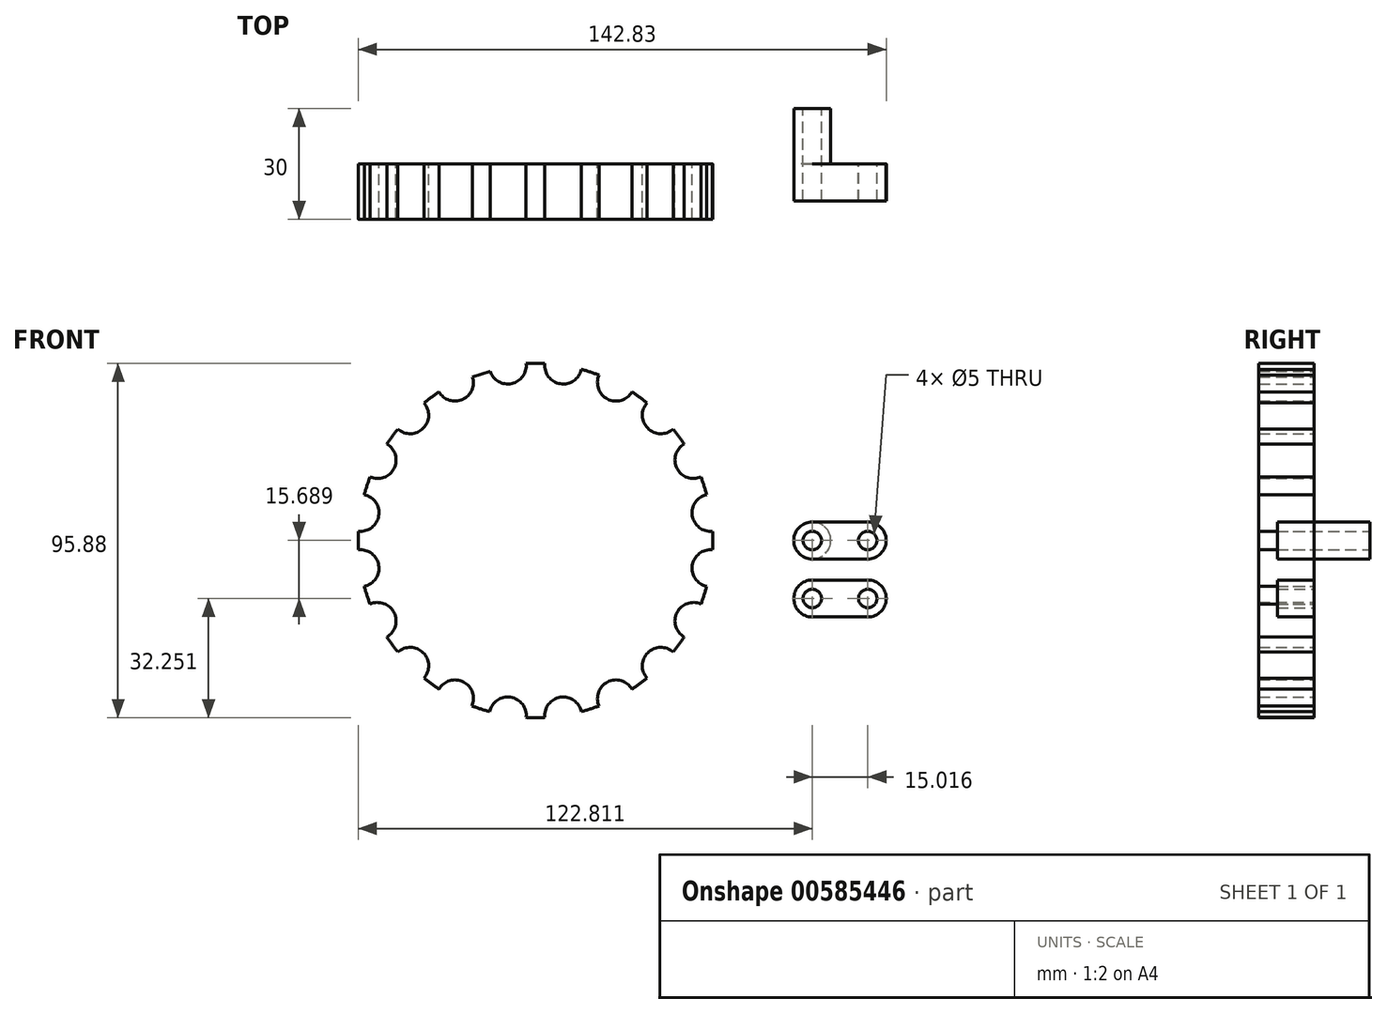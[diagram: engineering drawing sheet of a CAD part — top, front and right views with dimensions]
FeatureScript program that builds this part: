
annotation { "Feature Type Name" : "Feature", "Feature Type Description" : "" }
export const myFeature = defineFeature(function(context is Context, id is Id, definition is map)
    precondition{}
    {
        {
            var Q0;
            Q0=qCreatedBy(makeId("Front.planeOp"),FACE);
            var sketch = newSketch(context, id + "F0", { "sketchPlane" : qUnion([Q0])});
            skCircle(sketch, "E0.cCircle", {"center": v(0, 0) * mm, "radius": 47.35 * mm, "construction": true});
            skLineSegment(sketch, "E0.0", {"start": v(47.35, 7.5) * mm, "end": v(47.35, -7.5) * mm});
            skLineSegment(sketch, "E0.1", {"start": v(47.35, -7.5) * mm, "end": v(42.72, -21.77) * mm});
            skLineSegment(sketch, "E0.2", {"start": v(42.72, -21.77) * mm, "end": v(33.9, -33.9) * mm});
            skLineSegment(sketch, "E0.3", {"start": v(33.9, -33.9) * mm, "end": v(21.77, -42.72) * mm});
            skLineSegment(sketch, "E0.4", {"start": v(21.77, -42.72) * mm, "end": v(7.5, -47.35) * mm});
            skLineSegment(sketch, "E0.5", {"start": v(7.5, -47.35) * mm, "end": v(-7.5, -47.35) * mm});
            skLineSegment(sketch, "E0.6", {"start": v(-7.5, -47.35) * mm, "end": v(-21.77, -42.72) * mm});
            skLineSegment(sketch, "E0.7", {"start": v(-21.77, -42.72) * mm, "end": v(-33.9, -33.9) * mm});
            skLineSegment(sketch, "E0.8", {"start": v(-33.9, -33.9) * mm, "end": v(-42.72, -21.77) * mm});
            skLineSegment(sketch, "E0.9", {"start": v(-42.72, -21.77) * mm, "end": v(-47.35, -7.5) * mm});
            skLineSegment(sketch, "E0.10", {"start": v(-47.35, -7.5) * mm, "end": v(-47.35, 7.5) * mm});
            skLineSegment(sketch, "E0.11", {"start": v(-47.35, 7.5) * mm, "end": v(-42.72, 21.77) * mm});
            skLineSegment(sketch, "E0.12", {"start": v(-42.72, 21.77) * mm, "end": v(-33.9, 33.9) * mm});
            skLineSegment(sketch, "E0.13", {"start": v(-33.9, 33.9) * mm, "end": v(-21.77, 42.72) * mm});
            skLineSegment(sketch, "E0.14", {"start": v(-21.77, 42.72) * mm, "end": v(-7.5, 47.35) * mm});
            skLineSegment(sketch, "E0.15", {"start": v(-7.5, 47.35) * mm, "end": v(7.5, 47.35) * mm});
            skLineSegment(sketch, "E0.16", {"start": v(7.5, 47.35) * mm, "end": v(21.77, 42.72) * mm});
            skLineSegment(sketch, "E0.17", {"start": v(21.77, 42.72) * mm, "end": v(33.9, 33.9) * mm});
            skLineSegment(sketch, "E0.18", {"start": v(33.9, 33.9) * mm, "end": v(42.72, 21.77) * mm});
            skLineSegment(sketch, "E0.19", {"start": v(42.72, 21.77) * mm, "end": v(47.35, 7.5) * mm});
            skPoint(sketch, "E0.0.midPoint", {"position": v(47.35, 0) * mm});
            skCircle(sketch, "E1", {"center": v(47.35, 7.5) * mm, "radius": 5 * mm});
            skCircle(sketch, "E2.1.0", {"center": v(42.72, 21.77) * mm, "radius": 5 * mm});
            skCircle(sketch, "E2.2.0", {"center": v(33.9, 33.9) * mm, "radius": 5 * mm});
            skCircle(sketch, "E2.3.0", {"center": v(21.77, 42.72) * mm, "radius": 5 * mm});
            skCircle(sketch, "E3.1.4.0", {"center": v(7.5, 47.35) * mm, "radius": 5 * mm});
            skCircle(sketch, "E3.1.5.0", {"center": v(-7.5, 47.35) * mm, "radius": 5 * mm});
            skCircle(sketch, "E3.1.6.0", {"center": v(-21.77, 42.72) * mm, "radius": 5 * mm});
            skCircle(sketch, "E3.1.7.0", {"center": v(-33.9, 33.9) * mm, "radius": 5 * mm});
            skCircle(sketch, "E3.1.8.0", {"center": v(-42.72, 21.77) * mm, "radius": 5 * mm});
            skCircle(sketch, "E3.1.9.0", {"center": v(-47.35, 7.5) * mm, "radius": 5 * mm});
            skCircle(sketch, "E3.1.10.0", {"center": v(-47.35, -7.5) * mm, "radius": 5 * mm});
            skCircle(sketch, "E3.1.11.0", {"center": v(-42.72, -21.77) * mm, "radius": 5 * mm});
            skCircle(sketch, "E3.1.12.0", {"center": v(-33.9, -33.9) * mm, "radius": 5 * mm});
            skCircle(sketch, "E3.1.13.0", {"center": v(-21.77, -42.72) * mm, "radius": 5 * mm});
            skCircle(sketch, "E3.1.14.0", {"center": v(-7.5, -47.35) * mm, "radius": 5 * mm});
            skCircle(sketch, "E3.1.15.0", {"center": v(7.5, -47.35) * mm, "radius": 5 * mm});
            skCircle(sketch, "E3.1.16.0", {"center": v(21.77, -42.72) * mm, "radius": 5 * mm});
            skCircle(sketch, "E3.1.17.0", {"center": v(33.9, -33.9) * mm, "radius": 5 * mm});
            skCircle(sketch, "E3.1.18.0", {"center": v(42.72, -21.77) * mm, "radius": 5 * mm});
            skCircle(sketch, "E3.1.19.0", {"center": v(47.35, -7.5) * mm, "radius": 5 * mm});
            skCircle(sketch, "E4", {"center": v(74.87, 0) * mm, "radius": 5 * mm});
            skCircle(sketch, "E5", {"center": v(89.87, 0) * mm, "radius": 5 * mm});
            skLineSegment(sketch, "E6", {"start": v(74.87, 0) * mm, "end": v(89.87, 0) * mm, "construction": true});
            skLineSegment(sketch, "E7.bottom", {"start": v(74.87, 5) * mm, "end": v(89.87, 5) * mm});
            skLineSegment(sketch, "E7.top", {"start": v(74.87, -5) * mm, "end": v(89.87, -5) * mm});
            skLineSegment(sketch, "E7.left", {"start": v(74.87, 5) * mm, "end": v(74.87, -5) * mm});
            skLineSegment(sketch, "E7.right", {"start": v(89.87, 5) * mm, "end": v(89.87, -5) * mm});
            skCircle(sketch, "E8", {"center": v(74.87, 0) * mm, "radius": 2.5 * mm});
            skCircle(sketch, "E9", {"center": v(89.87, 0) * mm, "radius": 2.5 * mm});
            skCircle(sketch, "E10", {"center": v(74.89, -15.69) * mm, "radius": 2.5 * mm});
            skCircle(sketch, "E11", {"center": v(74.89, -15.69) * mm, "radius": 5 * mm});
            skLineSegment(sketch, "E12", {"start": v(74.89, -15.69) * mm, "end": v(89.89, -15.69) * mm, "construction": true});
            skCircle(sketch, "E13", {"center": v(89.89, -15.69) * mm, "radius": 5 * mm});
            skCircle(sketch, "E14", {"center": v(89.89, -15.69) * mm, "radius": 2.5 * mm});
            skLineSegment(sketch, "E15.bottom", {"start": v(74.89, -10.69) * mm, "end": v(89.89, -10.69) * mm});
            skLineSegment(sketch, "E15.top", {"start": v(74.89, -20.69) * mm, "end": v(89.89, -20.69) * mm});
            skLineSegment(sketch, "E15.left", {"start": v(74.89, -10.69) * mm, "end": v(74.89, -20.69) * mm});
            skLineSegment(sketch, "E15.right", {"start": v(89.89, -10.69) * mm, "end": v(89.89, -20.69) * mm});
            skCircle(sketch, "E16", {"center": v(0, 0) * mm, "radius": 47.94 * mm});
            skSolve(sketch);
        }
        {
            var Q0;
            {var subQ3=sQuery(id+"F0.wireOp",EDGE,"E1");var subQ39=sQuery(id+"F0.wireOp",EDGE,"E0.0");var subQ40=makeQuery(id+"F0.imprint","INTERSECT",VERTEX,{"derivedFrom":[subQ39,subQ3]});Q0=makeQuery(id+"F0.imprint","IMPRINT",FACE,{"disambiguationData":[TD([[makeQuery(id+"F0.imprint","IMPRINT",EDGE,{"disambiguationData":[TD([[subQ40,-1.0]])],"derivedFrom":subQ39}),-1.0]])]});}
            var Q1;
            {var subQ0=sQuery(id+"F0.wireOp",EDGE,"E2.1.0");var subQ1=sQuery(id+"F0.wireOp",EDGE,"E0.19");var subQ2=makeQuery(id+"F0.imprint","INTERSECT",VERTEX,{"derivedFrom":[subQ1,subQ0]});Q1=makeQuery(id+"F0.imprint","IMPRINT",FACE,{"disambiguationData":[TD([[makeQuery(id+"F0.imprint","IMPRINT",EDGE,{"disambiguationData":[TD([[subQ2,-1.0]])],"derivedFrom":subQ1}),1.0]])]});}
            var Q2;
            {var subQ0=sQuery(id+"F0.wireOp",EDGE,"E1");var subQ1=sQuery(id+"F0.wireOp",EDGE,"E0.0");var subQ2=makeQuery(id+"F0.imprint","INTERSECT",VERTEX,{"derivedFrom":[subQ1,subQ0]});Q2=makeQuery(id+"F0.imprint","IMPRINT",FACE,{"disambiguationData":[TD([[makeQuery(id+"F0.imprint","IMPRINT",EDGE,{"disambiguationData":[TD([[subQ2,-1.0]])],"derivedFrom":subQ1}),1.0]])]});}
            var Q3;
            {var subQ0=sQuery(id+"F0.wireOp",EDGE,"E2.2.0");var subQ1=sQuery(id+"F0.wireOp",EDGE,"E0.18");var subQ2=makeQuery(id+"F0.imprint","INTERSECT",VERTEX,{"derivedFrom":[subQ1,subQ0]});Q3=makeQuery(id+"F0.imprint","IMPRINT",FACE,{"disambiguationData":[TD([[makeQuery(id+"F0.imprint","IMPRINT",EDGE,{"disambiguationData":[TD([[subQ2,-1.0]])],"derivedFrom":subQ1}),1.0]])]});}
            var Q4;
            {var subQ0=sQuery(id+"F0.wireOp",EDGE,"E2.3.0");var subQ1=sQuery(id+"F0.wireOp",EDGE,"E0.17");var subQ2=makeQuery(id+"F0.imprint","INTERSECT",VERTEX,{"derivedFrom":[subQ1,subQ0]});Q4=makeQuery(id+"F0.imprint","IMPRINT",FACE,{"disambiguationData":[TD([[makeQuery(id+"F0.imprint","IMPRINT",EDGE,{"disambiguationData":[TD([[subQ2,-1.0]])],"derivedFrom":subQ1}),1.0]])]});}
            var Q5;
            {var subQ0=sQuery(id+"F0.wireOp",EDGE,"E3.1.4.0");var subQ1=sQuery(id+"F0.wireOp",EDGE,"E0.16");var subQ2=makeQuery(id+"F0.imprint","INTERSECT",VERTEX,{"derivedFrom":[subQ1,subQ0]});Q5=makeQuery(id+"F0.imprint","IMPRINT",FACE,{"disambiguationData":[TD([[makeQuery(id+"F0.imprint","IMPRINT",EDGE,{"disambiguationData":[TD([[subQ2,-1.0]])],"derivedFrom":subQ1}),1.0]])]});}
            var Q6;
            {var subQ0=sQuery(id+"F0.wireOp",EDGE,"E3.1.5.0");var subQ1=sQuery(id+"F0.wireOp",EDGE,"E0.15");var subQ2=makeQuery(id+"F0.imprint","INTERSECT",VERTEX,{"derivedFrom":[subQ1,subQ0]});Q6=makeQuery(id+"F0.imprint","IMPRINT",FACE,{"disambiguationData":[TD([[makeQuery(id+"F0.imprint","IMPRINT",EDGE,{"disambiguationData":[TD([[subQ2,-1.0]])],"derivedFrom":subQ1}),1.0]])]});}
            var Q7;
            {var subQ0=sQuery(id+"F0.wireOp",EDGE,"E3.1.7.0");var subQ1=sQuery(id+"F0.wireOp",EDGE,"E0.13");var subQ2=makeQuery(id+"F0.imprint","INTERSECT",VERTEX,{"derivedFrom":[subQ1,subQ0]});Q7=makeQuery(id+"F0.imprint","IMPRINT",FACE,{"disambiguationData":[TD([[makeQuery(id+"F0.imprint","IMPRINT",EDGE,{"disambiguationData":[TD([[subQ2,-1.0]])],"derivedFrom":subQ1}),1.0]])]});}
            var Q8;
            {var subQ0=sQuery(id+"F0.wireOp",EDGE,"E3.1.8.0");var subQ1=sQuery(id+"F0.wireOp",EDGE,"E0.12");var subQ2=makeQuery(id+"F0.imprint","INTERSECT",VERTEX,{"derivedFrom":[subQ1,subQ0]});Q8=makeQuery(id+"F0.imprint","IMPRINT",FACE,{"disambiguationData":[TD([[makeQuery(id+"F0.imprint","IMPRINT",EDGE,{"disambiguationData":[TD([[subQ2,-1.0]])],"derivedFrom":subQ1}),1.0]])]});}
            var Q9;
            {var subQ0=sQuery(id+"F0.wireOp",EDGE,"E3.1.9.0");var subQ1=sQuery(id+"F0.wireOp",EDGE,"E0.11");var subQ2=makeQuery(id+"F0.imprint","INTERSECT",VERTEX,{"derivedFrom":[subQ1,subQ0]});Q9=makeQuery(id+"F0.imprint","IMPRINT",FACE,{"disambiguationData":[TD([[makeQuery(id+"F0.imprint","IMPRINT",EDGE,{"disambiguationData":[TD([[subQ2,-1.0]])],"derivedFrom":subQ1}),1.0]])]});}
            var Q10;
            {var subQ0=sQuery(id+"F0.wireOp",EDGE,"E3.1.10.0");var subQ1=sQuery(id+"F0.wireOp",EDGE,"E0.10");var subQ2=makeQuery(id+"F0.imprint","INTERSECT",VERTEX,{"derivedFrom":[subQ1,subQ0]});Q10=makeQuery(id+"F0.imprint","IMPRINT",FACE,{"disambiguationData":[TD([[makeQuery(id+"F0.imprint","IMPRINT",EDGE,{"disambiguationData":[TD([[subQ2,-1.0]])],"derivedFrom":subQ1}),1.0]])]});}
            var Q11;
            {var subQ0=sQuery(id+"F0.wireOp",EDGE,"E3.1.11.0");var subQ1=sQuery(id+"F0.wireOp",EDGE,"E0.9");var subQ2=makeQuery(id+"F0.imprint","INTERSECT",VERTEX,{"derivedFrom":[subQ1,subQ0]});Q11=makeQuery(id+"F0.imprint","IMPRINT",FACE,{"disambiguationData":[TD([[makeQuery(id+"F0.imprint","IMPRINT",EDGE,{"disambiguationData":[TD([[subQ2,-1.0]])],"derivedFrom":subQ1}),1.0]])]});}
            var Q12;
            {var subQ0=sQuery(id+"F0.wireOp",EDGE,"E3.1.12.0");var subQ1=sQuery(id+"F0.wireOp",EDGE,"E0.8");var subQ2=makeQuery(id+"F0.imprint","INTERSECT",VERTEX,{"derivedFrom":[subQ1,subQ0]});Q12=makeQuery(id+"F0.imprint","IMPRINT",FACE,{"disambiguationData":[TD([[makeQuery(id+"F0.imprint","IMPRINT",EDGE,{"disambiguationData":[TD([[subQ2,-1.0]])],"derivedFrom":subQ1}),1.0]])]});}
            var Q13;
            {var subQ0=sQuery(id+"F0.wireOp",EDGE,"E3.1.13.0");var subQ1=sQuery(id+"F0.wireOp",EDGE,"E0.7");var subQ2=makeQuery(id+"F0.imprint","INTERSECT",VERTEX,{"derivedFrom":[subQ1,subQ0]});Q13=makeQuery(id+"F0.imprint","IMPRINT",FACE,{"disambiguationData":[TD([[makeQuery(id+"F0.imprint","IMPRINT",EDGE,{"disambiguationData":[TD([[subQ2,-1.0]])],"derivedFrom":subQ1}),1.0]])]});}
            var Q14;
            {var subQ0=sQuery(id+"F0.wireOp",EDGE,"E3.1.14.0");var subQ1=sQuery(id+"F0.wireOp",EDGE,"E0.6");var subQ2=makeQuery(id+"F0.imprint","INTERSECT",VERTEX,{"derivedFrom":[subQ1,subQ0]});Q14=makeQuery(id+"F0.imprint","IMPRINT",FACE,{"disambiguationData":[TD([[makeQuery(id+"F0.imprint","IMPRINT",EDGE,{"disambiguationData":[TD([[subQ2,-1.0]])],"derivedFrom":subQ1}),1.0]])]});}
            var Q15;
            {var subQ0=sQuery(id+"F0.wireOp",EDGE,"E3.1.15.0");var subQ1=sQuery(id+"F0.wireOp",EDGE,"E0.5");var subQ2=makeQuery(id+"F0.imprint","INTERSECT",VERTEX,{"derivedFrom":[subQ1,subQ0]});Q15=makeQuery(id+"F0.imprint","IMPRINT",FACE,{"disambiguationData":[TD([[makeQuery(id+"F0.imprint","IMPRINT",EDGE,{"disambiguationData":[TD([[subQ2,-1.0]])],"derivedFrom":subQ1}),1.0]])]});}
            var Q16;
            {var subQ0=sQuery(id+"F0.wireOp",EDGE,"E3.1.16.0");var subQ1=sQuery(id+"F0.wireOp",EDGE,"E0.4");var subQ2=makeQuery(id+"F0.imprint","INTERSECT",VERTEX,{"derivedFrom":[subQ1,subQ0]});Q16=makeQuery(id+"F0.imprint","IMPRINT",FACE,{"disambiguationData":[TD([[makeQuery(id+"F0.imprint","IMPRINT",EDGE,{"disambiguationData":[TD([[subQ2,-1.0]])],"derivedFrom":subQ1}),1.0]])]});}
            var Q17;
            {var subQ0=sQuery(id+"F0.wireOp",EDGE,"E3.1.17.0");var subQ1=sQuery(id+"F0.wireOp",EDGE,"E0.3");var subQ2=makeQuery(id+"F0.imprint","INTERSECT",VERTEX,{"derivedFrom":[subQ1,subQ0]});Q17=makeQuery(id+"F0.imprint","IMPRINT",FACE,{"disambiguationData":[TD([[makeQuery(id+"F0.imprint","IMPRINT",EDGE,{"disambiguationData":[TD([[subQ2,-1.0]])],"derivedFrom":subQ1}),1.0]])]});}
            var Q18;
            {var subQ0=sQuery(id+"F0.wireOp",EDGE,"E3.1.18.0");var subQ1=sQuery(id+"F0.wireOp",EDGE,"E0.2");var subQ2=makeQuery(id+"F0.imprint","INTERSECT",VERTEX,{"derivedFrom":[subQ1,subQ0]});Q18=makeQuery(id+"F0.imprint","IMPRINT",FACE,{"disambiguationData":[TD([[makeQuery(id+"F0.imprint","IMPRINT",EDGE,{"disambiguationData":[TD([[subQ2,-1.0]])],"derivedFrom":subQ1}),1.0]])]});}
            var Q19;
            {var subQ0=sQuery(id+"F0.wireOp",EDGE,"E3.1.19.0");var subQ1=sQuery(id+"F0.wireOp",EDGE,"E0.1");var subQ2=makeQuery(id+"F0.imprint","INTERSECT",VERTEX,{"derivedFrom":[subQ1,subQ0]});Q19=makeQuery(id+"F0.imprint","IMPRINT",FACE,{"disambiguationData":[TD([[makeQuery(id+"F0.imprint","IMPRINT",EDGE,{"disambiguationData":[TD([[subQ2,-1.0]])],"derivedFrom":subQ1}),1.0]])]});}
            extrude(context, id + "F1", {"entities" : qUnion([Q0, Q1, Q2, Q3, Q4, Q5, Q6, Q7, Q8, Q9, Q10, Q11, Q12, Q13, Q14, Q15, Q16, Q17, Q18, Q19]), "depth" : 15 * mm, "offsetDistance" : 25 * mm});
        }
        {
            var Q0;
            {var subQ1=sQuery(id+"F0.wireOp",EDGE,"E7.bottom");Q0=makeQuery(id+"F0.imprint","IMPRINT",FACE,{"disambiguationData":[TD([[makeQuery(id+"F0.imprint","IMPRINT",EDGE,{"derivedFrom":subQ1}),-1.0]])]});}
            var Q1;
            {var subQ0=sQuery(id+"F0.wireOp",EDGE,"E7.left");var subQ4=sQuery(id+"F0.wireOp",EDGE,"E8");var subQ5=makeQuery(id+"F0.imprint","INTERSECT",VERTEX,{"disambiguationData":[OD(0.0)],"derivedFrom":[subQ0,subQ4]});Q1=makeQuery(id+"F0.imprint","IMPRINT",FACE,{"disambiguationData":[TD([[makeQuery(id+"F0.imprint","IMPRINT",EDGE,{"disambiguationData":[TD([[subQ5,1.0]])],"derivedFrom":subQ4}),-1.0]])]});}
            var Q2;
            {var subQ0=sQuery(id+"F0.wireOp",EDGE,"E7.left");var subQ4=sQuery(id+"F0.wireOp",EDGE,"E8");var subQ5=makeQuery(id+"F0.imprint","INTERSECT",VERTEX,{"disambiguationData":[OD(0.0)],"derivedFrom":[subQ0,subQ4]});Q2=makeQuery(id+"F0.imprint","IMPRINT",FACE,{"disambiguationData":[TD([[makeQuery(id+"F0.imprint","IMPRINT",EDGE,{"disambiguationData":[TD([[subQ5,-1.0]])],"derivedFrom":subQ4}),-1.0]])]});}
            var Q3;
            {var subQ0=sQuery(id+"F0.wireOp",EDGE,"E7.right");var subQ4=sQuery(id+"F0.wireOp",EDGE,"E9");var subQ5=makeQuery(id+"F0.imprint","INTERSECT",VERTEX,{"disambiguationData":[OD(0.0)],"derivedFrom":[subQ0,subQ4]});Q3=makeQuery(id+"F0.imprint","IMPRINT",FACE,{"disambiguationData":[TD([[makeQuery(id+"F0.imprint","IMPRINT",EDGE,{"disambiguationData":[TD([[subQ5,-1.0]])],"derivedFrom":subQ4}),-1.0]])]});}
            var Q4;
            {var subQ0=sQuery(id+"F0.wireOp",EDGE,"E7.right");var subQ4=sQuery(id+"F0.wireOp",EDGE,"E9");var subQ5=makeQuery(id+"F0.imprint","INTERSECT",VERTEX,{"disambiguationData":[OD(0.0)],"derivedFrom":[subQ0,subQ4]});Q4=makeQuery(id+"F0.imprint","IMPRINT",FACE,{"disambiguationData":[TD([[makeQuery(id+"F0.imprint","IMPRINT",EDGE,{"disambiguationData":[TD([[subQ5,1.0]])],"derivedFrom":subQ4}),-1.0]])]});}
            extrude(context, id + "F2", {"entities" : qUnion([Q0, Q1, Q2, Q3, Q4]), "depth" : 10 * mm, "offsetDistance" : 25 * mm});
        }
        {
            var Q0;
            {var subQ0=sQuery(id+"F0.wireOp",EDGE,"E7.left");var subQ4=sQuery(id+"F0.wireOp",EDGE,"E8");var subQ5=makeQuery(id+"F0.imprint","INTERSECT",VERTEX,{"disambiguationData":[OD(0.0)],"derivedFrom":[subQ0,subQ4]});Q0=makeQuery(id+"F0.imprint","IMPRINT",FACE,{"disambiguationData":[TD([[makeQuery(id+"F0.imprint","IMPRINT",EDGE,{"disambiguationData":[TD([[subQ5,-1.0]])],"derivedFrom":subQ4}),-1.0]])]});}
            var Q1;
            {var subQ0=sQuery(id+"F0.wireOp",EDGE,"E7.left");var subQ4=sQuery(id+"F0.wireOp",EDGE,"E8");var subQ5=makeQuery(id+"F0.imprint","INTERSECT",VERTEX,{"disambiguationData":[OD(0.0)],"derivedFrom":[subQ0,subQ4]});Q1=makeQuery(id+"F0.imprint","IMPRINT",FACE,{"disambiguationData":[TD([[makeQuery(id+"F0.imprint","IMPRINT",EDGE,{"disambiguationData":[TD([[subQ5,1.0]])],"derivedFrom":subQ4}),-1.0]])]});}
            extrude(context, id + "F3", {"entities" : qUnion([Q0, Q1]), "operationType" : NewBodyOperationType.ADD, "oppositeDirection" : true, "depth" : 15 * mm, "offsetDistance" : 25 * mm});
        }
        {
            var Q0;
            {var subQ1=sQuery(id+"F0.wireOp",EDGE,"E15.bottom");Q0=makeQuery(id+"F0.imprint","IMPRINT",FACE,{"disambiguationData":[TD([[makeQuery(id+"F0.imprint","IMPRINT",EDGE,{"derivedFrom":subQ1}),-1.0]])]});}
            var Q1;
            {var subQ0=sQuery(id+"F0.wireOp",EDGE,"E15.left");var subQ1=sQuery(id+"F0.wireOp",EDGE,"E10");var subQ2=makeQuery(id+"F0.imprint","INTERSECT",VERTEX,{"disambiguationData":[OD(0.0)],"derivedFrom":[subQ1,subQ0]});Q1=makeQuery(id+"F0.imprint","IMPRINT",FACE,{"disambiguationData":[TD([[makeQuery(id+"F0.imprint","IMPRINT",EDGE,{"disambiguationData":[TD([[subQ2,1.0]])],"derivedFrom":subQ1}),-1.0]])]});}
            var Q2;
            {var subQ0=sQuery(id+"F0.wireOp",EDGE,"E15.left");var subQ1=sQuery(id+"F0.wireOp",EDGE,"E10");var subQ2=makeQuery(id+"F0.imprint","INTERSECT",VERTEX,{"disambiguationData":[OD(0.0)],"derivedFrom":[subQ1,subQ0]});Q2=makeQuery(id+"F0.imprint","IMPRINT",FACE,{"disambiguationData":[TD([[makeQuery(id+"F0.imprint","IMPRINT",EDGE,{"disambiguationData":[TD([[subQ2,-1.0]])],"derivedFrom":subQ1}),-1.0]])]});}
            var Q3;
            {var subQ0=sQuery(id+"F0.wireOp",EDGE,"E15.right");var subQ4=sQuery(id+"F0.wireOp",EDGE,"E14");var subQ5=makeQuery(id+"F0.imprint","INTERSECT",VERTEX,{"disambiguationData":[OD(0.0)],"derivedFrom":[subQ4,subQ0]});Q3=makeQuery(id+"F0.imprint","IMPRINT",FACE,{"disambiguationData":[TD([[makeQuery(id+"F0.imprint","IMPRINT",EDGE,{"disambiguationData":[TD([[subQ5,-1.0]])],"derivedFrom":subQ4}),-1.0]])]});}
            var Q4;
            {var subQ0=sQuery(id+"F0.wireOp",EDGE,"E15.right");var subQ4=sQuery(id+"F0.wireOp",EDGE,"E14");var subQ6=makeQuery(id+"F0.imprint","INTERSECT",VERTEX,{"disambiguationData":[OD(0.0)],"derivedFrom":[subQ4,subQ0]});Q4=makeQuery(id+"F0.imprint","IMPRINT",FACE,{"disambiguationData":[TD([[makeQuery(id+"F0.imprint","IMPRINT",EDGE,{"disambiguationData":[TD([[subQ6,1.0]])],"derivedFrom":subQ4}),-1.0]])]});}
            extrude(context, id + "F4", {"entities" : qUnion([Q0, Q1, Q2, Q3, Q4]), "depth" : 10 * mm, "offsetDistance" : 25 * mm});
        }
    });
